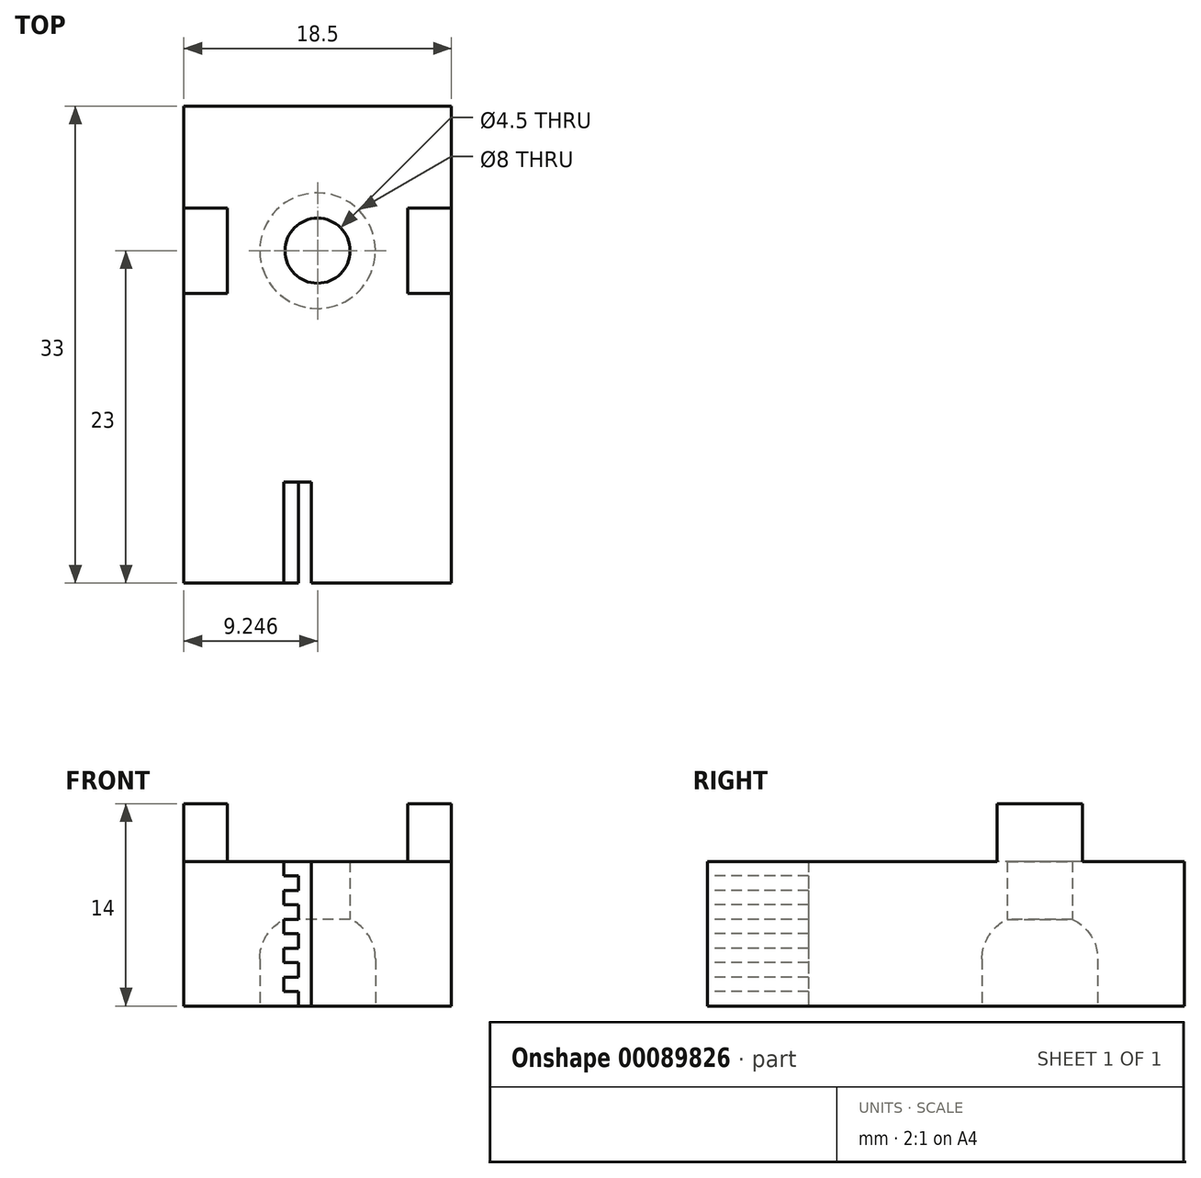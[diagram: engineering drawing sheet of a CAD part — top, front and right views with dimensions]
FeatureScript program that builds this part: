
annotation { "Feature Type Name" : "Feature", "Feature Type Description" : "" }
export const myFeature = defineFeature(function(context is Context, id is Id, definition is map)
    precondition{}
    {
        {
            var Q0;
            Q0=qCreatedBy(makeId("Top.planeOp"),FACE);
            var sketch = newSketch(context, id + "F0", { "sketchPlane" : qUnion([Q0])});
            skLineSegment(sketch, "E0.bottom", {"start": v(-4.96, 0) * mm, "end": v(13.54, 0) * mm});
            skLineSegment(sketch, "E0.top", {"start": v(-4.96, 33) * mm, "end": v(13.54, 33) * mm});
            skLineSegment(sketch, "E0.left", {"start": v(-4.96, 0) * mm, "end": v(-4.96, 33) * mm});
            skLineSegment(sketch, "E0.right", {"start": v(13.54, 0) * mm, "end": v(13.54, 33) * mm});
            skLineSegment(sketch, "E1", {"start": v(-4.96, 13) * mm, "end": v(13.54, 13) * mm});
            skLineSegment(sketch, "E2.bottom", {"start": v(-4.96, 25.95) * mm, "end": v(-1.96, 25.95) * mm});
            skLineSegment(sketch, "E2.top", {"start": v(-4.96, 20.05) * mm, "end": v(-1.96, 20.05) * mm});
            skLineSegment(sketch, "E2.left", {"start": v(-4.96, 25.95) * mm, "end": v(-4.96, 20.05) * mm});
            skLineSegment(sketch, "E2.right", {"start": v(-1.96, 25.95) * mm, "end": v(-1.96, 20.05) * mm});
            skLineSegment(sketch, "E3.bottom", {"start": v(13.54, 25.95) * mm, "end": v(10.54, 25.95) * mm});
            skLineSegment(sketch, "E3.top", {"start": v(13.54, 20.05) * mm, "end": v(10.54, 20.05) * mm});
            skLineSegment(sketch, "E3.left", {"start": v(13.54, 25.95) * mm, "end": v(13.54, 20.05) * mm});
            skLineSegment(sketch, "E3.right", {"start": v(10.54, 25.95) * mm, "end": v(10.54, 20.05) * mm});
            skCircle(sketch, "E4", {"center": v(4.29, 23) * mm, "radius": 2.25 * mm});
            skPoint(sketch, "E5", {"position": v(-1.96, 23) * mm});
            skPoint(sketch, "E6", {"position": v(-4.96, 23) * mm});
            skLineSegment(sketch, "E7", {"start": v(-4.96, 23) * mm, "end": v(13.54, 23) * mm});
            skSolve(sketch);
        }
        {
            var Q0;
            {var subQ2=sQuery(id+"F0.wireOp",EDGE,"E0.top");Q0=makeQuery(id+"F0.imprint","IMPRINT",FACE,{"disambiguationData":[TD([[makeQuery(id+"F0.imprint","IMPRINT",EDGE,{"derivedFrom":subQ2}),-1.0]])]});}
            var Q1;
            {var subQ1=sQuery(id+"F0.wireOp",EDGE,"E1");Q1=makeQuery(id+"F0.imprint","IMPRINT",FACE,{"disambiguationData":[TD([[makeQuery(id+"F0.imprint","IMPRINT",EDGE,{"derivedFrom":subQ1}),1.0]])]});}
            var Q2;
            {var subQ0=sQuery(id+"F0.wireOp",EDGE,"E0.bottom");Q2=makeQuery(id+"F0.imprint","IMPRINT",FACE,{"disambiguationData":[TD([[makeQuery(id+"F0.imprint","IMPRINT",EDGE,{"derivedFrom":subQ0}),1.0]])]});}
            extrude(context, id + "F1", {"entities" : qUnion([Q0, Q1, Q2]), "depth" : 10 * mm});
        }
        {
            var Q0;
            {var subQ0=sQuery(id+"F0.wireOp",EDGE,"E2.top");Q0=makeQuery(id+"F0.imprint","IMPRINT",FACE,{"disambiguationData":[TD([[makeQuery(id+"F0.imprint","IMPRINT",EDGE,{"derivedFrom":subQ0}),1.0]])]});}
            var Q1;
            {var subQ0=sQuery(id+"F0.wireOp",EDGE,"E2.bottom");Q1=makeQuery(id+"F0.imprint","IMPRINT",FACE,{"disambiguationData":[TD([[makeQuery(id+"F0.imprint","IMPRINT",EDGE,{"derivedFrom":subQ0}),-1.0]])]});}
            var Q2;
            {var subQ0=sQuery(id+"F0.wireOp",EDGE,"E3.bottom");Q2=makeQuery(id+"F0.imprint","IMPRINT",FACE,{"disambiguationData":[TD([[makeQuery(id+"F0.imprint","IMPRINT",EDGE,{"derivedFrom":subQ0}),1.0]])]});}
            var Q3;
            {var subQ0=sQuery(id+"F0.wireOp",EDGE,"E3.top");Q3=makeQuery(id+"F0.imprint","IMPRINT",FACE,{"disambiguationData":[TD([[makeQuery(id+"F0.imprint","IMPRINT",EDGE,{"derivedFrom":subQ0}),-1.0]])]});}
            extrude(context, id + "F2", {"entities" : qUnion([Q0, Q1, Q2, Q3]), "operationType" : NewBodyOperationType.ADD, "depth" : 14 * mm});
        }
        {
            var Q0;
            Q0=makeQuery(id+"F1.opExtrude","SWEPT_FACE",FACE,{"disambiguationData":[OSD([sQuery(id+"F0.wireOp",EDGE,"E0.bottom")])]});
            var sketch = newSketch(context, id + "F3", { "sketchPlane" : qUnion([Q0])});
            skLineSegment(sketch, "E8", {"start": v(1.96, 10) * mm, "end": v(1.96, 9) * mm});
            skLineSegment(sketch, "E9", {"start": v(1.96, 9) * mm, "end": v(2.96, 9) * mm});
            skLineSegment(sketch, "E10", {"start": v(2.96, 9) * mm, "end": v(2.96, 8) * mm});
            skLineSegment(sketch, "E11", {"start": v(2.96, 8) * mm, "end": v(1.96, 8) * mm});
            skLineSegment(sketch, "E12", {"start": v(1.96, 8) * mm, "end": v(1.96, 7) * mm});
            skLineSegment(sketch, "E13", {"start": v(1.96, 7) * mm, "end": v(2.96, 7) * mm});
            skLineSegment(sketch, "E14", {"start": v(2.96, 7) * mm, "end": v(2.96, 6) * mm});
            skLineSegment(sketch, "E15", {"start": v(2.96, 6) * mm, "end": v(1.96, 6) * mm});
            skLineSegment(sketch, "E16", {"start": v(1.96, 6) * mm, "end": v(1.96, 5) * mm});
            skLineSegment(sketch, "E17", {"start": v(1.96, 5) * mm, "end": v(2.96, 5) * mm});
            skLineSegment(sketch, "E18", {"start": v(2.96, 5) * mm, "end": v(2.96, 4) * mm});
            skLineSegment(sketch, "E19", {"start": v(2.96, 4) * mm, "end": v(1.96, 4) * mm});
            skLineSegment(sketch, "E20", {"start": v(1.96, 4) * mm, "end": v(1.96, 3) * mm});
            skLineSegment(sketch, "E21", {"start": v(1.96, 3) * mm, "end": v(2.96, 3) * mm});
            skLineSegment(sketch, "E22", {"start": v(2.96, 3) * mm, "end": v(2.96, 2) * mm});
            skLineSegment(sketch, "E23", {"start": v(2.96, 2) * mm, "end": v(1.96, 2) * mm});
            skLineSegment(sketch, "E24", {"start": v(1.96, 2) * mm, "end": v(1.96, 1) * mm});
            skLineSegment(sketch, "E25", {"start": v(1.96, 1) * mm, "end": v(2.96, 1) * mm});
            skLineSegment(sketch, "E26", {"start": v(2.96, 1) * mm, "end": v(2.96, 0) * mm});
            skLineSegment(sketch, "E27", {"start": v(2.96, 0) * mm, "end": v(1.96, 0) * mm});
            skLineSegment(sketch, "E28", {"start": v(3.86, 10) * mm, "end": v(3.86, 0) * mm});
            skLineSegment(sketch, "E29", {"start": v(1.96, 10) * mm, "end": v(3.86, 10) * mm});
            skLineSegment(sketch, "E30", {"start": v(3.86, 0) * mm, "end": v(2.96, 0) * mm});
            skSolve(sketch);
        }
        {
            var Q0;
            Q0=makeQuery(id+"F3.imprint","IMPRINT",FACE,{"disambiguationData":[TD([[makeQuery(id+"F3.imprint","IMPRINT",EDGE,{"derivedFrom":sQuery(id+"F3.wireOp",EDGE,"E8")}),1.0]])]});
            extrude(context, id + "F4", {"entities" : qUnion([Q0]), "operationType" : NewBodyOperationType.REMOVE, "oppositeDirection" : true, "depth" : 7 * mm});
        }
        {
            var Q0;
            {var subQ0=sQuery(id+"F0.wireOp",EDGE,"E3.right");var subQ1=sQuery(id+"F0.wireOp",EDGE,"E3.top");var subQ2=sQuery(id+"F0.wireOp",EDGE,"E3.bottom");var subQ3=sQuery(id+"F0.wireOp",EDGE,"E2.right");var subQ4=sQuery(id+"F0.wireOp",EDGE,"E2.top");var subQ5=sQuery(id+"F0.wireOp",EDGE,"E2.bottom");Q0=makeQuery(id+"F2.boolean.opBoolean","MERGE",FACE,{"derivedFrom":[makeQuery(id+"F1.opExtrude","CAP_FACE",FACE,{"disambiguationData":[OSD([sQuery(id+"F0.wireOp",EDGE,"E0.bottom"),sQuery(id+"F0.wireOp",EDGE,"E0.top"),sQuery(id+"F0.wireOp",EDGE,"E0.left"),sQuery(id+"F0.wireOp",EDGE,"E0.right"),subQ5,subQ4,subQ3,subQ2,subQ1,subQ0,sQuery(id+"F0.wireOp",EDGE,"E4")])],"isStart":true}),makeQuery(id+"F2.opExtrude","CAP_FACE",FACE,{"disambiguationData":[OSD([subQ5,subQ4,sQuery(id+"F0.wireOp",EDGE,"E2.left"),subQ3])],"isStart":true}),makeQuery(id+"F2.opExtrude","CAP_FACE",FACE,{"disambiguationData":[OSD([subQ2,subQ1,sQuery(id+"F0.wireOp",EDGE,"E3.left"),subQ0])],"isStart":true})]});}
            var sketch = newSketch(context, id + "F5", { "sketchPlane" : qUnion([Q0])});
            skCircle(sketch, "E31", {"center": v(4.29, -23) * mm, "radius": 4 * mm});
            skSolve(sketch);
        }
        {
            var Q0;
            Q0=makeQuery(id+"F5.imprint","IMPRINT",FACE,{"disambiguationData":[TD([[makeQuery(id+"F5.imprint","IMPRINT",EDGE,{"derivedFrom":sQuery(id+"F5.wireOp",EDGE,"E31")}),1.0]])]});
            extrude(context, id + "F6", {"entities" : qUnion([Q0]), "operationType" : NewBodyOperationType.REMOVE, "oppositeDirection" : true, "depth" : 6 * mm});
        }
        {
            var Q0;
            Q0=makeQuery(id+"F6.boolean.opBoolean","COPY",EDGE,{"derivedFrom":makeQuery(id+"F6.opExtrude","CAP_EDGE",EDGE,{"disambiguationData":[OSD([sQuery(id+"F5.wireOp",EDGE,"E31")])],"isStart":false})});
            fillet(context, id + "F7", {"entities" : qUnion([Q0]), "radius" : 3 * mm, "tangentPropagation" : true, "allowEdgeOverflow" : false});
        }
    });
